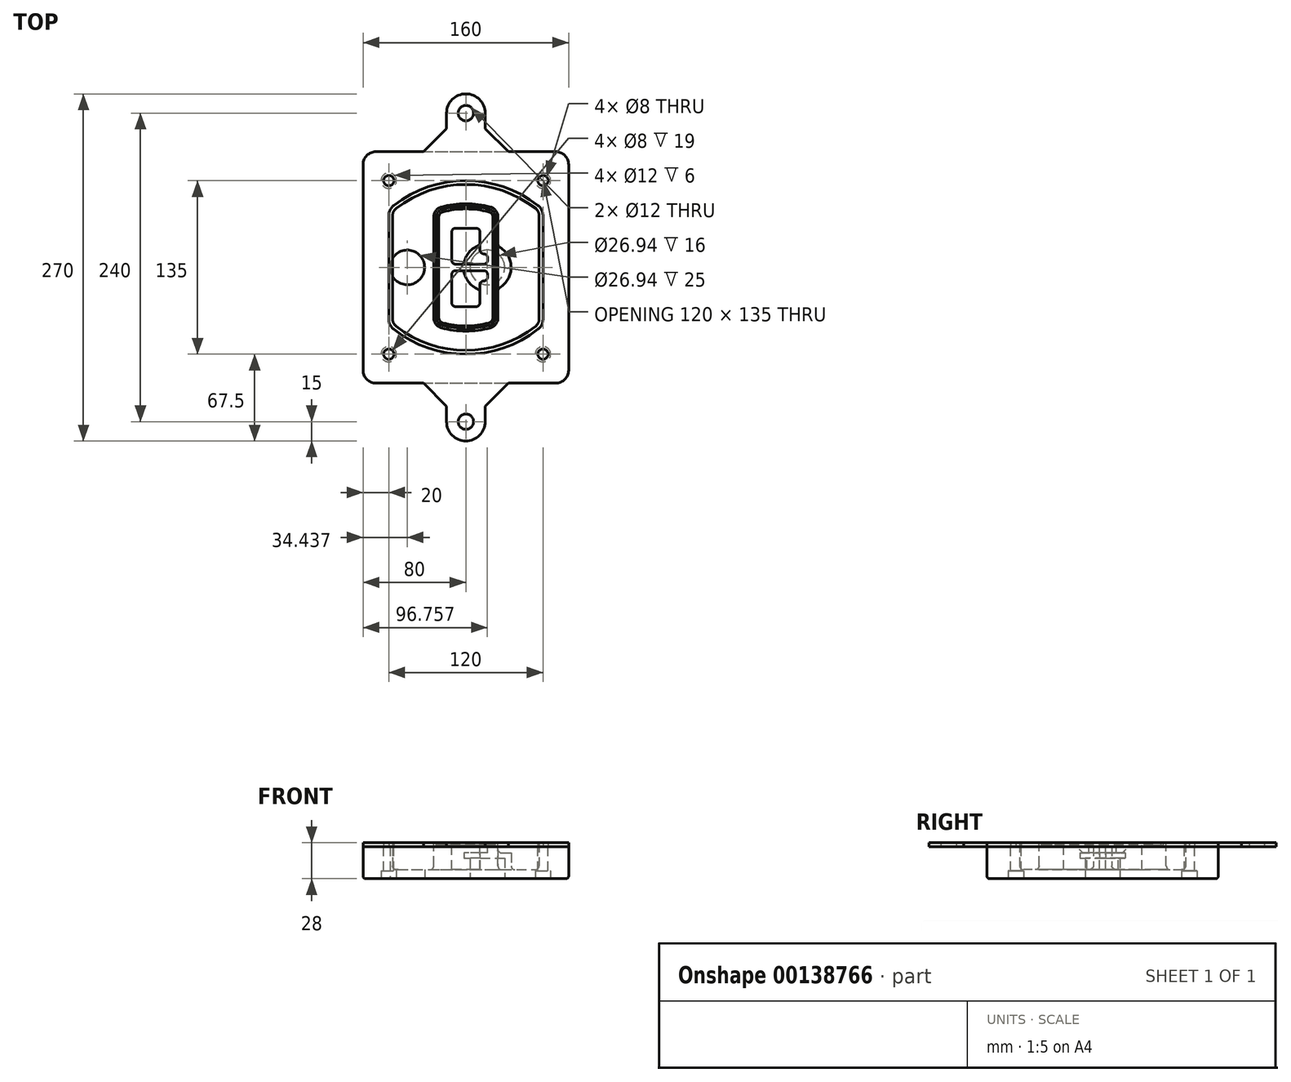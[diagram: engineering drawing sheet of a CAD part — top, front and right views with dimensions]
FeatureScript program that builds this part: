
annotation { "Feature Type Name" : "Feature", "Feature Type Description" : "" }
export const myFeature = defineFeature(function(context is Context, id is Id, definition is map)
    precondition{}
    {
        {
            var Q0;
            Q0=qCreatedBy(makeId("Top.planeOp"),FACE);
            var sketch = newSketch(context, id + "F0", { "sketchPlane" : qUnion([Q0])});
            skPoint(sketch, "E0.rect.middle", {"position": v(0, 0) * mm});
            skLineSegment(sketch, "E1.bottom", {"start": v(-70, -90) * mm, "end": v(70, -90) * mm});
            skLineSegment(sketch, "E1.top", {"start": v(-70, 90) * mm, "end": v(70, 90) * mm});
            skLineSegment(sketch, "E1.left", {"start": v(-80, -80) * mm, "end": v(-80, 80) * mm});
            skLineSegment(sketch, "E1.right", {"start": v(80, -80) * mm, "end": v(80, 80) * mm});
            skLineSegment(sketch, "E2", {"start": v(-80, 90) * mm, "end": v(80, -90) * mm, "construction": true});
            skLineSegment(sketch, "E3", {"start": v(80, 90) * mm, "end": v(-80, -90) * mm, "construction": true});
            skCircle(sketch, "E4", {"center": v(-60, 67.5) * mm, "radius": 4 * mm});
            skCircle(sketch, "E5", {"center": v(60, 67.5) * mm, "radius": 4 * mm});
            skCircle(sketch, "E6", {"center": v(60, -67.5) * mm, "radius": 4 * mm});
            skCircle(sketch, "E7", {"center": v(-60, -67.5) * mm, "radius": 4 * mm});
            skLineSegment(sketch, "E8", {"start": v(-60, 67.5) * mm, "end": v(60, 67.5) * mm, "construction": true});
            skLineSegment(sketch, "E9", {"start": v(60, 67.5) * mm, "end": v(60, -67.5) * mm, "construction": true});
            skLineSegment(sketch, "E10", {"start": v(60, -67.5) * mm, "end": v(-60, -67.5) * mm, "construction": true});
            skLineSegment(sketch, "E11", {"start": v(-60, -67.5) * mm, "end": v(-60, 67.5) * mm, "construction": true});
            skLineSegment(sketch, "E12", {"start": v(-60, 40.3) * mm, "end": v(-60, -40.3) * mm});
            skLineSegment(sketch, "E13", {"start": v(60, 40.3) * mm, "end": v(60, -40.3) * mm});
            skArc(sketch, "E14", {"start": v(56.15, 48.18) * mm, "mid": v(0, 67.5) * mm, "end": v(-56.15, 48.18) * mm});
            skArc(sketch, "E15", {"start": v(-56.15, -48.18) * mm, "mid": v(0, -67.5) * mm, "end": v(56.15, -48.18) * mm});
            skLineSegment(sketch, "E16", {"start": v(-60, 0) * mm, "end": v(60, 0) * mm, "construction": true});
            skPoint(sketch, "E17.visualSharp", {"position": v(-60, -45) * mm});
            skArc(sketch, "E17.filletArc", {"start": v(-60, -40.3) * mm, "mid": v(-58.99, -44.68) * mm, "end": v(-56.15, -48.18) * mm});
            skPoint(sketch, "E18.visualSharp", {"position": v(-60, 45) * mm});
            skArc(sketch, "E18.filletArc", {"start": v(-56.15, 48.18) * mm, "mid": v(-58.99, 44.68) * mm, "end": v(-60, 40.3) * mm});
            skPoint(sketch, "E19.visualSharp", {"position": v(60, 45) * mm});
            skArc(sketch, "E19.filletArc", {"start": v(60, 40.3) * mm, "mid": v(58.99, 44.68) * mm, "end": v(56.15, 48.18) * mm});
            skPoint(sketch, "E20.visualSharp", {"position": v(60, -45) * mm});
            skArc(sketch, "E20.filletArc", {"start": v(56.15, -48.18) * mm, "mid": v(58.99, -44.68) * mm, "end": v(60, -40.3) * mm});
            skPoint(sketch, "E21.visualSharp", {"position": v(-80, 90) * mm});
            skArc(sketch, "E21.filletArc", {"start": v(-70, 90) * mm, "mid": v(-77.07, 87.07) * mm, "end": v(-80, 80) * mm});
            skPoint(sketch, "E22.visualSharp", {"position": v(80, 90) * mm});
            skArc(sketch, "E22.filletArc", {"start": v(80, 80) * mm, "mid": v(77.07, 87.07) * mm, "end": v(70, 90) * mm});
            skPoint(sketch, "E23.visualSharp", {"position": v(80, -90) * mm});
            skArc(sketch, "E23.filletArc", {"start": v(70, -90) * mm, "mid": v(77.07, -87.07) * mm, "end": v(80, -80) * mm});
            skPoint(sketch, "E24.visualSharp", {"position": v(-80, -90) * mm});
            skArc(sketch, "E24.filletArc", {"start": v(-80, -80) * mm, "mid": v(-77.07, -87.07) * mm, "end": v(-70, -90) * mm});
            skArc(sketch, "E25.0", {"start": v(57, 40.3) * mm, "mid": v(56.3, 43.36) * mm, "end": v(54.3, 45.81) * mm});
            skLineSegment(sketch, "E25.1", {"start": v(57, 40.3) * mm, "end": v(57, -40.3) * mm});
            skArc(sketch, "E25.2", {"start": v(54.3, -45.81) * mm, "mid": v(56.3, -43.36) * mm, "end": v(57, -40.3) * mm});
            skArc(sketch, "E25.3", {"start": v(-54.3, -45.81) * mm, "mid": v(0, -64.5) * mm, "end": v(54.3, -45.81) * mm});
            skArc(sketch, "E25.4", {"start": v(-57, -40.3) * mm, "mid": v(-56.3, -43.36) * mm, "end": v(-54.3, -45.81) * mm});
            skArc(sketch, "E25.5", {"start": v(54.3, 45.81) * mm, "mid": v(0, 64.5) * mm, "end": v(-54.3, 45.81) * mm});
            skLineSegment(sketch, "E25.6", {"start": v(-57, 40.3) * mm, "end": v(-57, -40.3) * mm});
            skArc(sketch, "E25.7", {"start": v(-54.3, 45.81) * mm, "mid": v(-56.3, 43.36) * mm, "end": v(-57, 40.3) * mm});
            skArc(sketch, "E26.0", {"start": v(-58.62, 51.33) * mm, "mid": v(-62.58, 46.43) * mm, "end": v(-64, 40.3) * mm});
            skArc(sketch, "E26.1", {"start": v(58.62, 51.33) * mm, "mid": v(0, 71.5) * mm, "end": v(-58.62, 51.33) * mm});
            skArc(sketch, "E26.2", {"start": v(64, 40.3) * mm, "mid": v(62.58, 46.43) * mm, "end": v(58.62, 51.33) * mm});
            skLineSegment(sketch, "E26.3", {"start": v(64, 40.3) * mm, "end": v(64, -40.3) * mm});
            skArc(sketch, "E26.4", {"start": v(58.62, -51.33) * mm, "mid": v(62.58, -46.43) * mm, "end": v(64, -40.3) * mm});
            skLineSegment(sketch, "E26.5", {"start": v(-64, 40.3) * mm, "end": v(-64, -40.3) * mm});
            skArc(sketch, "E26.6", {"start": v(-58.62, -51.33) * mm, "mid": v(0, -71.5) * mm, "end": v(58.62, -51.33) * mm});
            skArc(sketch, "E26.7", {"start": v(-64, -40.3) * mm, "mid": v(-62.58, -46.43) * mm, "end": v(-58.62, -51.33) * mm});
            skSolve(sketch);
        }
        {
            var Q0;
            Q0=makeQuery(id+"F0.imprint","IMPRINT",FACE,{"disambiguationData":[TD([[makeQuery(id+"F0.imprint","IMPRINT",EDGE,{"derivedFrom":sQuery(id+"F0.wireOp",EDGE,"E1.bottom")}),1.0]])]});
            var Q1;
            Q1=makeQuery(id+"F0.imprint","IMPRINT",FACE,{"disambiguationData":[TD([[makeQuery(id+"F0.imprint","IMPRINT",EDGE,{"derivedFrom":sQuery(id+"F0.wireOp",EDGE,"E12")}),1.0]])]});
            var Q2;
            Q2=makeQuery(id+"F0.imprint","IMPRINT",FACE,{"disambiguationData":[TD([[makeQuery(id+"F0.imprint","IMPRINT",EDGE,{"derivedFrom":sQuery(id+"F0.wireOp",EDGE,"E25.0")}),1.0]])]});
            var Q3;
            Q3=makeQuery(id+"F0.imprint","IMPRINT",FACE,{"disambiguationData":[TD([[makeQuery(id+"F0.imprint","IMPRINT",EDGE,{"derivedFrom":sQuery(id+"F0.wireOp",EDGE,"E12")}),-1.0]])]});
            extrude(context, id + "F1", {"entities" : qUnion([Q0, Q1, Q2, Q3]), "oppositeDirection" : true, "depth" : 25 * mm});
        }
        {
            var Q0;
            Q0=makeQuery(id+"F0.imprint","IMPRINT",FACE,{"disambiguationData":[TD([[makeQuery(id+"F0.imprint","IMPRINT",EDGE,{"derivedFrom":sQuery(id+"F0.wireOp",EDGE,"E12")}),1.0]])]});
            extrude(context, id + "F2", {"entities" : qUnion([Q0]), "operationType" : NewBodyOperationType.ADD, "depth" : 3 * mm});
        }
        {
            var Q0;
            Q0=makeQuery(id+"F0.imprint","IMPRINT",FACE,{"disambiguationData":[TD([[makeQuery(id+"F0.imprint","IMPRINT",EDGE,{"derivedFrom":sQuery(id+"F0.wireOp",EDGE,"E25.0")}),1.0]])]});
            extrude(context, id + "F3", {"entities" : qUnion([Q0]), "operationType" : NewBodyOperationType.REMOVE, "oppositeDirection" : true, "depth" : 18 * mm});
        }
        {
            var Q0;
            Q0=makeQuery(id+"F2.opExtrude","CAP_FACE",FACE,{"disambiguationData":[OSD([sQuery(id+"F0.wireOp",EDGE,"E12"),sQuery(id+"F0.wireOp",EDGE,"E13"),sQuery(id+"F0.wireOp",EDGE,"E14"),sQuery(id+"F0.wireOp",EDGE,"E15"),sQuery(id+"F0.wireOp",EDGE,"E17.filletArc"),sQuery(id+"F0.wireOp",EDGE,"E18.filletArc"),sQuery(id+"F0.wireOp",EDGE,"E19.filletArc"),sQuery(id+"F0.wireOp",EDGE,"E20.filletArc"),sQuery(id+"F0.wireOp",EDGE,"E25.0"),sQuery(id+"F0.wireOp",EDGE,"E25.1"),sQuery(id+"F0.wireOp",EDGE,"E25.2"),sQuery(id+"F0.wireOp",EDGE,"E25.3"),sQuery(id+"F0.wireOp",EDGE,"E25.4"),sQuery(id+"F0.wireOp",EDGE,"E25.5"),sQuery(id+"F0.wireOp",EDGE,"E25.6"),sQuery(id+"F0.wireOp",EDGE,"E25.7")])],"isStart":false});
            var sketch = newSketch(context, id + "F4", { "sketchPlane" : qUnion([Q0])});
            skArc(sketch, "E27.0", {"start": v(-19.08, -46.97) * mm, "mid": v(0, -49.5) * mm, "end": v(19.08, -46.97) * mm});
            skArc(sketch, "E28.0", {"start": v(19.08, 46.97) * mm, "mid": v(0, 49.5) * mm, "end": v(-19.08, 46.97) * mm});
            skLineSegment(sketch, "E29", {"start": v(-25, 39.25) * mm, "end": v(-25, -39.25) * mm});
            skLineSegment(sketch, "E30", {"start": v(25, 39.25) * mm, "end": v(25, -39.25) * mm});
            skLineSegment(sketch, "E31", {"start": v(-25, 45.1) * mm, "end": v(25, 45.1) * mm, "construction": true});
            skLineSegment(sketch, "E32", {"start": v(-25, -45.1) * mm, "end": v(25, -45.1) * mm, "construction": true});
            skPoint(sketch, "E33.visualSharp", {"position": v(-25, 45.1) * mm});
            skArc(sketch, "E33.filletArc", {"start": v(-19.08, 46.97) * mm, "mid": v(-23.35, 44.11) * mm, "end": v(-25, 39.25) * mm});
            skPoint(sketch, "E34.visualSharp", {"position": v(25, 45.1) * mm});
            skArc(sketch, "E34.filletArc", {"start": v(25, 39.25) * mm, "mid": v(23.35, 44.11) * mm, "end": v(19.08, 46.97) * mm});
            skPoint(sketch, "E35.visualSharp", {"position": v(25, -45.1) * mm});
            skArc(sketch, "E35.filletArc", {"start": v(19.08, -46.97) * mm, "mid": v(23.35, -44.11) * mm, "end": v(25, -39.25) * mm});
            skPoint(sketch, "E36.visualSharp", {"position": v(-25, -45.1) * mm});
            skArc(sketch, "E36.filletArc", {"start": v(-25, -39.25) * mm, "mid": v(-23.35, -44.11) * mm, "end": v(-19.08, -46.97) * mm});
            skArc(sketch, "E37.0", {"start": v(54.3, 45.81) * mm, "mid": v(0, 64.5) * mm, "end": v(-54.3, 45.81) * mm});
            skArc(sketch, "E37.1", {"start": v(-54.3, 45.81) * mm, "mid": v(-56.3, 43.36) * mm, "end": v(-57, 40.3) * mm});
            skLineSegment(sketch, "E37.2", {"start": v(-57, 40.3) * mm, "end": v(-57, -40.3) * mm});
            skArc(sketch, "E37.3", {"start": v(-57, -40.3) * mm, "mid": v(-56.3, -43.36) * mm, "end": v(-54.3, -45.81) * mm});
            skArc(sketch, "E37.4", {"start": v(-54.3, -45.81) * mm, "mid": v(0, -64.5) * mm, "end": v(54.3, -45.81) * mm});
            skArc(sketch, "E37.5", {"start": v(54.3, -45.81) * mm, "mid": v(56.3, -43.36) * mm, "end": v(57, -40.3) * mm});
            skLineSegment(sketch, "E37.6", {"start": v(57, 40.3) * mm, "end": v(57, -40.3) * mm});
            skArc(sketch, "E37.7", {"start": v(57, 40.3) * mm, "mid": v(56.3, 43.36) * mm, "end": v(54.3, 45.81) * mm});
            skLineSegment(sketch, "E38.0", {"start": v(23, 39.25) * mm, "end": v(23, -39.25) * mm});
            skArc(sketch, "E38.1", {"start": v(18.56, -45.04) * mm, "mid": v(21.76, -42.9) * mm, "end": v(23, -39.25) * mm});
            skArc(sketch, "E38.2", {"start": v(-18.56, -45.04) * mm, "mid": v(0, -47.5) * mm, "end": v(18.56, -45.04) * mm});
            skArc(sketch, "E38.3", {"start": v(-23, -39.25) * mm, "mid": v(-21.76, -42.9) * mm, "end": v(-18.56, -45.04) * mm});
            skLineSegment(sketch, "E38.4", {"start": v(-23, 39.25) * mm, "end": v(-23, -39.25) * mm});
            skArc(sketch, "E38.5", {"start": v(23, 39.25) * mm, "mid": v(21.76, 42.9) * mm, "end": v(18.56, 45.04) * mm});
            skArc(sketch, "E38.6", {"start": v(-18.56, 45.04) * mm, "mid": v(-21.76, 42.9) * mm, "end": v(-23, 39.25) * mm});
            skArc(sketch, "E38.7", {"start": v(18.56, 45.04) * mm, "mid": v(0, 47.5) * mm, "end": v(-18.56, 45.04) * mm});
            skArc(sketch, "E39.0", {"start": v(21, 39.25) * mm, "mid": v(20.18, 41.68) * mm, "end": v(18.04, 43.1) * mm});
            skLineSegment(sketch, "E39.1", {"start": v(21, 39.25) * mm, "end": v(21, -39.25) * mm});
            skArc(sketch, "E39.2", {"start": v(18.04, -43.1) * mm, "mid": v(20.18, -41.68) * mm, "end": v(21, -39.25) * mm});
            skArc(sketch, "E39.3", {"start": v(-18.04, -43.1) * mm, "mid": v(0, -45.5) * mm, "end": v(18.04, -43.1) * mm});
            skArc(sketch, "E39.4", {"start": v(-21, -39.25) * mm, "mid": v(-20.18, -41.68) * mm, "end": v(-18.04, -43.1) * mm});
            skArc(sketch, "E39.5", {"start": v(18.04, 43.1) * mm, "mid": v(0, 45.5) * mm, "end": v(-18.04, 43.1) * mm});
            skLineSegment(sketch, "E39.6", {"start": v(-21, 39.25) * mm, "end": v(-21, -39.25) * mm});
            skArc(sketch, "E39.7", {"start": v(-18.04, 43.1) * mm, "mid": v(-20.18, 41.68) * mm, "end": v(-21, 39.25) * mm});
            skLineSegment(sketch, "E40", {"start": v(-25, 0) * mm, "end": v(25, 0) * mm, "construction": true});
            skLineSegment(sketch, "E41", {"start": v(-11, 5.5) * mm, "end": v(-11, 27.5) * mm});
            skLineSegment(sketch, "E42", {"start": v(-8, 30.5) * mm, "end": v(8, 30.5) * mm});
            skLineSegment(sketch, "E43", {"start": v(11, 27.5) * mm, "end": v(11, 13.5) * mm});
            skLineSegment(sketch, "E44", {"start": v(14, 10.5) * mm, "end": v(14, 10.5) * mm});
            skLineSegment(sketch, "E45", {"start": v(17, 7.5) * mm, "end": v(17, 5.5) * mm});
            skLineSegment(sketch, "E46", {"start": v(14, 2.5) * mm, "end": v(-8, 2.5) * mm});
            skPoint(sketch, "E47.visualSharp", {"position": v(-11, 30.5) * mm});
            skArc(sketch, "E47.filletArc", {"start": v(-8, 30.5) * mm, "mid": v(-10.12, 29.62) * mm, "end": v(-11, 27.5) * mm});
            skPoint(sketch, "E48.visualSharp", {"position": v(11, 30.5) * mm});
            skArc(sketch, "E48.filletArc", {"start": v(11, 27.5) * mm, "mid": v(10.12, 29.62) * mm, "end": v(8, 30.5) * mm});
            skPoint(sketch, "E49.visualSharp", {"position": v(11, 10.5) * mm});
            skArc(sketch, "E49.filletArc", {"start": v(11, 13.5) * mm, "mid": v(11.88, 11.38) * mm, "end": v(14, 10.5) * mm});
            skPoint(sketch, "E50.visualSharp", {"position": v(17, 10.5) * mm});
            skArc(sketch, "E50.filletArc", {"start": v(17, 7.5) * mm, "mid": v(16.12, 9.62) * mm, "end": v(14, 10.5) * mm});
            skPoint(sketch, "E51.visualSharp", {"position": v(17, 2.5) * mm});
            skArc(sketch, "E51.filletArc", {"start": v(14, 2.5) * mm, "mid": v(16.12, 3.38) * mm, "end": v(17, 5.5) * mm});
            skPoint(sketch, "E52.visualSharp", {"position": v(-11, 2.5) * mm});
            skArc(sketch, "E52.filletArc", {"start": v(-11, 5.5) * mm, "mid": v(-10.12, 3.38) * mm, "end": v(-8, 2.5) * mm});
            skLineSegment(sketch, "E53.0.MirrorCS", {"start": v(14, -2.5) * mm, "end": v(-8, -2.5) * mm});
            skArc(sketch, "E54.0.MirrorCS", {"start": v(-11, -5.5) * mm, "mid": v(-10.12, -3.38) * mm, "end": v(-8, -2.5) * mm});
            skLineSegment(sketch, "E55.0.MirrorCS", {"start": v(-11, -5.5) * mm, "end": v(-11, -27.5) * mm});
            skArc(sketch, "E56.0.MirrorCS", {"start": v(-8, -30.5) * mm, "mid": v(-10.12, -29.62) * mm, "end": v(-11, -27.5) * mm});
            skLineSegment(sketch, "E57.0.MirrorCS", {"start": v(-8, -30.5) * mm, "end": v(8, -30.5) * mm});
            skArc(sketch, "E58.0.MirrorCS", {"start": v(11, -27.5) * mm, "mid": v(10.12, -29.62) * mm, "end": v(8, -30.5) * mm});
            skLineSegment(sketch, "E59.0.MirrorCS", {"start": v(11, -27.5) * mm, "end": v(11, -13.5) * mm});
            skArc(sketch, "E60.0.MirrorCS", {"start": v(11, -13.5) * mm, "mid": v(11.88, -11.38) * mm, "end": v(14, -10.5) * mm});
            skArc(sketch, "E61.0.MirrorCS", {"start": v(17, -7.5) * mm, "mid": v(16.12, -9.62) * mm, "end": v(14, -10.5) * mm});
            skLineSegment(sketch, "E62.0.MirrorCS", {"start": v(17, -7.5) * mm, "end": v(17, -5.5) * mm});
            skArc(sketch, "E63.0.MirrorCS", {"start": v(14, -2.5) * mm, "mid": v(16.12, -3.38) * mm, "end": v(17, -5.5) * mm});
            skSolve(sketch);
        }
        {
            var Q0;
            Q0=makeQuery(id+"F4.imprint","IMPRINT",FACE,{"disambiguationData":[TD([[makeQuery(id+"F4.imprint","IMPRINT",EDGE,{"derivedFrom":sQuery(id+"F4.wireOp",EDGE,"E27.0")}),1.0]])]});
            var Q1;
            Q1=makeQuery(id+"F4.imprint","IMPRINT",FACE,{"disambiguationData":[TD([[makeQuery(id+"F4.imprint","IMPRINT",EDGE,{"derivedFrom":sQuery(id+"F4.wireOp",EDGE,"E38.0")}),-1.0]])]});
            var Q2;
            Q2=makeQuery(id+"F4.imprint","IMPRINT",FACE,{"disambiguationData":[TD([[makeQuery(id+"F4.imprint","IMPRINT",EDGE,{"derivedFrom":sQuery(id+"F4.wireOp",EDGE,"E39.0")}),1.0]])]});
            extrude(context, id + "F5", {"entities" : qUnion([Q0, Q1, Q2]), "operationType" : NewBodyOperationType.ADD, "endBound" : BoundingType.UP_TO_NEXT, "oppositeDirection" : true, "depth" : 25 * mm});
        }
        {
            var Q0;
            Q0=makeQuery(id+"F4.imprint","IMPRINT",FACE,{"disambiguationData":[TD([[makeQuery(id+"F4.imprint","IMPRINT",EDGE,{"derivedFrom":sQuery(id+"F4.wireOp",EDGE,"E38.0")}),-1.0]])]});
            extrude(context, id + "F6", {"entities" : qUnion([Q0]), "operationType" : NewBodyOperationType.REMOVE, "oppositeDirection" : true, "depth" : 2 * mm});
        }
        {
            var Q0;
            Q0=makeQuery(id+"F1.opExtrude","CAP_FACE",FACE,{"disambiguationData":[OSD([sQuery(id+"F0.wireOp",EDGE,"E1.bottom"),sQuery(id+"F0.wireOp",EDGE,"E1.top"),sQuery(id+"F0.wireOp",EDGE,"E1.left"),sQuery(id+"F0.wireOp",EDGE,"E1.right"),sQuery(id+"F0.wireOp",EDGE,"E4"),sQuery(id+"F0.wireOp",EDGE,"E5"),sQuery(id+"F0.wireOp",EDGE,"E6"),sQuery(id+"F0.wireOp",EDGE,"E7"),sQuery(id+"F0.wireOp",EDGE,"E21.filletArc"),sQuery(id+"F0.wireOp",EDGE,"E22.filletArc"),sQuery(id+"F0.wireOp",EDGE,"E23.filletArc"),sQuery(id+"F0.wireOp",EDGE,"E24.filletArc")])],"isStart":false});
            var sketch = newSketch(context, id + "F7", { "sketchPlane" : qUnion([Q0])});
            skCircle(sketch, "E64", {"center": v(16.76, 0) * mm, "radius": 13.47 * mm});
            skCircle(sketch, "E65", {"center": v(-45.56, 0) * mm, "radius": 13.47 * mm});
            skLineSegment(sketch, "E66", {"start": v(80, 0) * mm, "end": v(-80, 0) * mm});
            skCircle(sketch, "E67", {"center": v(16.76, 0) * mm, "radius": 18.47 * mm});
            skCircle(sketch, "E68", {"center": v(60, -67.5) * mm, "radius": 6 * mm});
            skCircle(sketch, "E69", {"center": v(-60, -67.5) * mm, "radius": 6 * mm});
            skCircle(sketch, "E70", {"center": v(-60, 67.5) * mm, "radius": 6 * mm});
            skCircle(sketch, "E71", {"center": v(60, 67.5) * mm, "radius": 6 * mm});
            skSolve(sketch);
        }
        {
            var Q0;
            {var subQ1=sQuery(id+"F7.wireOp",EDGE,"E66");var subQ4=sQuery(id+"F7.wireOp",EDGE,"E64");var subQ6=makeQuery(id+"F7.imprint","INTERSECT",VERTEX,{"disambiguationData":[OD(0.0)],"derivedFrom":[subQ4,subQ1]});Q0=makeQuery(id+"F7.imprint","IMPRINT",FACE,{"disambiguationData":[TD([[makeQuery(id+"F7.imprint","IMPRINT",EDGE,{"disambiguationData":[TD([[subQ6,-1.0]])],"derivedFrom":subQ4}),-1.0]])]});}
            var Q1;
            {var subQ0=sQuery(id+"F7.wireOp",EDGE,"E66");var subQ1=sQuery(id+"F7.wireOp",EDGE,"E64");var subQ3=makeQuery(id+"F7.imprint","INTERSECT",VERTEX,{"disambiguationData":[OD(0.0)],"derivedFrom":[subQ1,subQ0]});Q1=makeQuery(id+"F7.imprint","IMPRINT",FACE,{"disambiguationData":[TD([[makeQuery(id+"F7.imprint","IMPRINT",EDGE,{"disambiguationData":[TD([[subQ3,-1.0]])],"derivedFrom":subQ1}),1.0]])]});}
            var Q2;
            {var subQ0=sQuery(id+"F7.wireOp",EDGE,"E66");var subQ1=sQuery(id+"F7.wireOp",EDGE,"E64");var subQ3=makeQuery(id+"F7.imprint","INTERSECT",VERTEX,{"disambiguationData":[OD(0.0)],"derivedFrom":[subQ1,subQ0]});Q2=makeQuery(id+"F7.imprint","IMPRINT",FACE,{"disambiguationData":[TD([[makeQuery(id+"F7.imprint","IMPRINT",EDGE,{"disambiguationData":[TD([[subQ3,1.0]])],"derivedFrom":subQ1}),1.0]])]});}
            var Q3;
            {var subQ1=sQuery(id+"F7.wireOp",EDGE,"E66");var subQ4=sQuery(id+"F7.wireOp",EDGE,"E64");var subQ6=makeQuery(id+"F7.imprint","INTERSECT",VERTEX,{"disambiguationData":[OD(0.0)],"derivedFrom":[subQ4,subQ1]});Q3=makeQuery(id+"F7.imprint","IMPRINT",FACE,{"disambiguationData":[TD([[makeQuery(id+"F7.imprint","IMPRINT",EDGE,{"disambiguationData":[TD([[subQ6,1.0]])],"derivedFrom":subQ4}),-1.0]])]});}
            extrude(context, id + "F8", {"entities" : qUnion([Q0, Q1, Q2, Q3]), "operationType" : NewBodyOperationType.ADD, "oppositeDirection" : true, "depth" : 20 * mm});
        }
        {
            var Q0;
            {var subQ0=sQuery(id+"F7.wireOp",EDGE,"E66");var subQ1=sQuery(id+"F7.wireOp",EDGE,"E64");var subQ3=makeQuery(id+"F7.imprint","INTERSECT",VERTEX,{"disambiguationData":[OD(0.0)],"derivedFrom":[subQ1,subQ0]});Q0=makeQuery(id+"F7.imprint","IMPRINT",FACE,{"disambiguationData":[TD([[makeQuery(id+"F7.imprint","IMPRINT",EDGE,{"disambiguationData":[TD([[subQ3,-1.0]])],"derivedFrom":subQ1}),1.0]])]});}
            var Q1;
            {var subQ0=sQuery(id+"F7.wireOp",EDGE,"E66");var subQ1=sQuery(id+"F7.wireOp",EDGE,"E64");var subQ3=makeQuery(id+"F7.imprint","INTERSECT",VERTEX,{"disambiguationData":[OD(0.0)],"derivedFrom":[subQ1,subQ0]});Q1=makeQuery(id+"F7.imprint","IMPRINT",FACE,{"disambiguationData":[TD([[makeQuery(id+"F7.imprint","IMPRINT",EDGE,{"disambiguationData":[TD([[subQ3,1.0]])],"derivedFrom":subQ1}),1.0]])]});}
            extrude(context, id + "F9", {"entities" : qUnion([Q0, Q1]), "operationType" : NewBodyOperationType.REMOVE, "oppositeDirection" : true, "depth" : 16 * mm});
        }
        {
            var Q0;
            {var subQ0=sQuery(id+"F7.wireOp",EDGE,"E66");var subQ1=sQuery(id+"F7.wireOp",EDGE,"E65");var subQ3=makeQuery(id+"F7.imprint","INTERSECT",VERTEX,{"disambiguationData":[OD(0.0)],"derivedFrom":[subQ1,subQ0]});Q0=makeQuery(id+"F7.imprint","IMPRINT",FACE,{"disambiguationData":[TD([[makeQuery(id+"F7.imprint","IMPRINT",EDGE,{"disambiguationData":[TD([[subQ3,-1.0]])],"derivedFrom":subQ1}),1.0]])]});}
            var Q1;
            {var subQ0=sQuery(id+"F7.wireOp",EDGE,"E66");var subQ1=sQuery(id+"F7.wireOp",EDGE,"E65");var subQ3=makeQuery(id+"F7.imprint","INTERSECT",VERTEX,{"disambiguationData":[OD(0.0)],"derivedFrom":[subQ1,subQ0]});Q1=makeQuery(id+"F7.imprint","IMPRINT",FACE,{"disambiguationData":[TD([[makeQuery(id+"F7.imprint","IMPRINT",EDGE,{"disambiguationData":[TD([[subQ3,1.0]])],"derivedFrom":subQ1}),1.0]])]});}
            extrude(context, id + "F10", {"entities" : qUnion([Q0, Q1]), "operationType" : NewBodyOperationType.REMOVE, "oppositeDirection" : true, "depth" : 25 * mm});
        }
        {
            var Q0;
            Q0=makeQuery(id+"F7.imprint","IMPRINT",FACE,{"disambiguationData":[TD([[makeQuery(id+"F7.imprint","IMPRINT",EDGE,{"derivedFrom":sQuery(id+"F7.wireOp",EDGE,"E68")}),1.0]])]});
            var Q1;
            Q1=makeQuery(id+"F7.imprint","IMPRINT",FACE,{"disambiguationData":[TD([[makeQuery(id+"F7.imprint","IMPRINT",EDGE,{"derivedFrom":makeQuery(id+"F1.opExtrude","CAP_EDGE",EDGE,{"disambiguationData":[OSD([sQuery(id+"F0.wireOp",EDGE,"E5")])],"isStart":false})}),-1.0]])]});
            var Q2;
            Q2=makeQuery(id+"F7.imprint","IMPRINT",FACE,{"disambiguationData":[TD([[makeQuery(id+"F7.imprint","IMPRINT",EDGE,{"derivedFrom":sQuery(id+"F7.wireOp",EDGE,"E69")}),1.0]])]});
            var Q3;
            Q3=makeQuery(id+"F7.imprint","IMPRINT",FACE,{"disambiguationData":[TD([[makeQuery(id+"F7.imprint","IMPRINT",EDGE,{"derivedFrom":makeQuery(id+"F1.opExtrude","CAP_EDGE",EDGE,{"disambiguationData":[OSD([sQuery(id+"F0.wireOp",EDGE,"E4")])],"isStart":false})}),-1.0]])]});
            var Q4;
            Q4=makeQuery(id+"F7.imprint","IMPRINT",FACE,{"disambiguationData":[TD([[makeQuery(id+"F7.imprint","IMPRINT",EDGE,{"derivedFrom":sQuery(id+"F7.wireOp",EDGE,"E70")}),1.0]])]});
            var Q5;
            Q5=makeQuery(id+"F7.imprint","IMPRINT",FACE,{"disambiguationData":[TD([[makeQuery(id+"F7.imprint","IMPRINT",EDGE,{"derivedFrom":makeQuery(id+"F1.opExtrude","CAP_EDGE",EDGE,{"disambiguationData":[OSD([sQuery(id+"F0.wireOp",EDGE,"E7")])],"isStart":false})}),-1.0]])]});
            var Q6;
            Q6=makeQuery(id+"F7.imprint","IMPRINT",FACE,{"disambiguationData":[TD([[makeQuery(id+"F7.imprint","IMPRINT",EDGE,{"derivedFrom":sQuery(id+"F7.wireOp",EDGE,"E71")}),1.0]])]});
            var Q7;
            Q7=makeQuery(id+"F7.imprint","IMPRINT",FACE,{"disambiguationData":[TD([[makeQuery(id+"F7.imprint","IMPRINT",EDGE,{"derivedFrom":makeQuery(id+"F1.opExtrude","CAP_EDGE",EDGE,{"disambiguationData":[OSD([sQuery(id+"F0.wireOp",EDGE,"E6")])],"isStart":false})}),-1.0]])]});
            extrude(context, id + "F11", {"entities" : qUnion([Q0, Q1, Q2, Q3, Q4, Q5, Q6, Q7]), "operationType" : NewBodyOperationType.REMOVE, "oppositeDirection" : true, "depth" : 6 * mm});
        }
        {
            var Q0;
            Q0=makeQuery(id+"F9.boolean.opBoolean","COPY",FACE,{"derivedFrom":makeQuery(id+"F9.opExtrude","CAP_FACE",FACE,{"disambiguationData":[OSD([sQuery(id+"F7.wireOp",EDGE,"E64")])],"isStart":false})});
            var sketch = newSketch(context, id + "F12", { "sketchPlane" : qUnion([Q0])});
            skArc(sketch, "E72.0", {"start": v(11, 17.55) * mm, "mid": v(2.57, 11.82) * mm, "end": v(-1.54, 2.5) * mm});
            skArc(sketch, "E72.1", {"start": v(-1.54, -2.5) * mm, "mid": v(2.57, -11.82) * mm, "end": v(11, -17.55) * mm});
            skLineSegment(sketch, "E73", {"start": v(-1.54, -2.5) * mm, "end": v(14, -2.5) * mm});
            skLineSegment(sketch, "E74.0", {"start": v(14, 2.5) * mm, "end": v(-1.54, 2.5) * mm});
            skArc(sketch, "E74.1", {"start": v(14, 2.5) * mm, "mid": v(16.12, 3.38) * mm, "end": v(17, 5.5) * mm});
            skLineSegment(sketch, "E74.2", {"start": v(17, 7.5) * mm, "end": v(17, 5.5) * mm});
            skArc(sketch, "E74.3", {"start": v(17, 7.5) * mm, "mid": v(16.12, 9.62) * mm, "end": v(14, 10.5) * mm});
            skArc(sketch, "E74.4", {"start": v(11, 13.5) * mm, "mid": v(11.88, 11.38) * mm, "end": v(14, 10.5) * mm});
            skLineSegment(sketch, "E74.5", {"start": v(11, 17.55) * mm, "end": v(11, 13.5) * mm});
            skLineSegment(sketch, "E74.7", {"start": v(14, -2.5) * mm, "end": v(-1.54, -2.5) * mm});
            skArc(sketch, "E74.8", {"start": v(14, -2.5) * mm, "mid": v(16.12, -3.38) * mm, "end": v(17, -5.5) * mm});
            skLineSegment(sketch, "E74.9", {"start": v(17, -7.5) * mm, "end": v(17, -5.5) * mm});
            skArc(sketch, "E74.10", {"start": v(17, -7.5) * mm, "mid": v(16.12, -9.62) * mm, "end": v(14, -10.5) * mm});
            skArc(sketch, "E74.11", {"start": v(11, -13.5) * mm, "mid": v(11.88, -11.38) * mm, "end": v(14, -10.5) * mm});
            skLineSegment(sketch, "E74.12", {"start": v(11, -17.55) * mm, "end": v(11, -13.5) * mm});
            skPoint(sketch, "E75.orphan", {"position": v(11, -27.5) * mm});
            skPoint(sketch, "E76.orphan", {"position": v(-8, -2.5) * mm});
            skPoint(sketch, "E77.orphan", {"position": v(-8, 2.5) * mm});
            skPoint(sketch, "E78.orphan", {"position": v(11, 27.5) * mm});
            skSolve(sketch);
        }
        {
            var Q0;
            {var subQ7=sQuery(id+"F12.wireOp",EDGE,"E72.0");var subQ14=sQuery(id+"F12.wireOp",EDGE,"E72.1");var subQ16=sQuery(id+"F12.wireOp",EDGE,"E74.1");var subQ18=sQuery(id+"F12.wireOp",EDGE,"E74.8");Q0=qUnion([makeQuery(id+"F12.imprint","IMPRINT",FACE,{"disambiguationData":[TD([[makeQuery(id+"F12.imprint","IMPRINT",EDGE,{"derivedFrom":subQ7}),1.0]])]}),makeQuery(id+"F12.imprint","IMPRINT",FACE,{"disambiguationData":[TD([[makeQuery(id+"F12.imprint","IMPRINT",EDGE,{"derivedFrom":subQ14}),1.0]])]}),makeQuery(id+"F12.imprint","IMPRINT",FACE,{"disambiguationData":[TD([[makeQuery(id+"F12.imprint","IMPRINT",EDGE,{"derivedFrom":subQ16}),1.0]])]}),makeQuery(id+"F12.imprint","IMPRINT",FACE,{"disambiguationData":[TD([[makeQuery(id+"F12.imprint","IMPRINT",EDGE,{"derivedFrom":subQ18}),-1.0]])]})]);}
            var Q1;
            Q1=makeQuery(id+"F5.boolean.opBoolean","SPLIT",FACE,{"disambiguationData":[TD([makeQuery(id+"F5.opExtrude","SWEPT_FACE",FACE,{"disambiguationData":[OSD([sQuery(id+"F4.wireOp",EDGE,"E41")])]})])],"derivedFrom":makeQuery(id+"F3.boolean.opBoolean","COPY",FACE,{"derivedFrom":makeQuery(id+"F3.opExtrude","CAP_FACE",FACE,{"disambiguationData":[OSD([sQuery(id+"F0.wireOp",EDGE,"E25.0"),sQuery(id+"F0.wireOp",EDGE,"E25.1"),sQuery(id+"F0.wireOp",EDGE,"E25.2"),sQuery(id+"F0.wireOp",EDGE,"E25.3"),sQuery(id+"F0.wireOp",EDGE,"E25.4"),sQuery(id+"F0.wireOp",EDGE,"E25.5"),sQuery(id+"F0.wireOp",EDGE,"E25.6"),sQuery(id+"F0.wireOp",EDGE,"E25.7")])],"isStart":false})})});
            extrude(context, id + "F13", {"entities" : qUnion([Q0]), "operationType" : NewBodyOperationType.REMOVE, "endBound" : BoundingType.UP_TO_SURFACE, "endBoundEntityFace" : qUnion([Q1]), "depth" : 25 * mm});
        }
        {
            var Q0;
            Q0=makeQuery(id+"F3.boolean.opBoolean","COPY",EDGE,{"derivedFrom":makeQuery(id+"F3.opExtrude","CAP_EDGE",EDGE,{"disambiguationData":[OSD([sQuery(id+"F0.wireOp",EDGE,"E25.6")])],"isStart":false})});
            var Q1;
            Q1=makeQuery(id+"F8.boolean.opBoolean","INTERSECT",EDGE,{"derivedFrom":[makeQuery(id+"F5.opExtrude","SWEPT_FACE",FACE,{"disambiguationData":[OSD([sQuery(id+"F4.wireOp",EDGE,"E30")])]}),makeQuery(id+"F8.opExtrude","CAP_FACE",FACE,{"disambiguationData":[OSD([sQuery(id+"F7.wireOp",EDGE,"E67")])],"isStart":false})]});
            var Q2;
            Q2=makeQuery(id+"F8.boolean.opBoolean","INTERSECT",EDGE,{"disambiguationData":[OD(1.0)],"derivedFrom":[makeQuery(id+"F5.opExtrude","SWEPT_FACE",FACE,{"disambiguationData":[OSD([sQuery(id+"F4.wireOp",EDGE,"E30")])]}),makeQuery(id+"F8.opExtrude","SWEPT_FACE",FACE,{"disambiguationData":[OSD([sQuery(id+"F7.wireOp",EDGE,"E67")])]})]});
            var Q3;
            {var subQ0=sQuery(id+"F4.wireOp",EDGE,"E30");Q3=makeQuery(id+"F8.boolean.opBoolean","SPLIT",EDGE,{"disambiguationData":[TD([makeQuery(id+"F5.opExtrude","SWEPT_FACE",FACE,{"disambiguationData":[OSD([sQuery(id+"F4.wireOp",EDGE,"E35.filletArc")])]})])],"derivedFrom":makeQuery(id+"F5.opExtrude","CAP_EDGE",EDGE,{"disambiguationData":[OSD([subQ0])],"isStart":false})});}
            var Q4;
            {var subQ0=sQuery(id+"F0.wireOp",EDGE,"E25.7");var subQ1=sQuery(id+"F0.wireOp",EDGE,"E25.1");var subQ2=sQuery(id+"F0.wireOp",EDGE,"E25.6");var subQ3=sQuery(id+"F0.wireOp",EDGE,"E25.5");var subQ4=sQuery(id+"F0.wireOp",EDGE,"E25.4");var subQ5=sQuery(id+"F0.wireOp",EDGE,"E25.0");var subQ6=sQuery(id+"F0.wireOp",EDGE,"E25.2");var subQ7=sQuery(id+"F0.wireOp",EDGE,"E25.3");Q4=makeQuery(id+"F8.boolean.opBoolean","INTERSECT",EDGE,{"derivedFrom":[makeQuery(id+"F5.boolean.opBoolean","SPLIT",FACE,{"disambiguationData":[TD([makeQuery(id+"F2.opExtrude","SWEPT_FACE",FACE,{"disambiguationData":[OSD([subQ5])]})])],"derivedFrom":makeQuery(id+"F3.boolean.opBoolean","COPY",FACE,{"derivedFrom":makeQuery(id+"F3.opExtrude","CAP_FACE",FACE,{"disambiguationData":[OSD([subQ5,subQ1,subQ6,subQ7,subQ4,subQ3,subQ2,subQ0])],"isStart":false})})}),makeQuery(id+"F8.opExtrude","SWEPT_FACE",FACE,{"disambiguationData":[OSD([sQuery(id+"F7.wireOp",EDGE,"E67")])]})]});}
            var Q5;
            Q5=makeQuery(id+"F8.boolean.opBoolean","INTERSECT",EDGE,{"disambiguationData":[OD(0.0)],"derivedFrom":[makeQuery(id+"F5.opExtrude","SWEPT_FACE",FACE,{"disambiguationData":[OSD([sQuery(id+"F4.wireOp",EDGE,"E30")])]}),makeQuery(id+"F8.opExtrude","SWEPT_FACE",FACE,{"disambiguationData":[OSD([sQuery(id+"F7.wireOp",EDGE,"E67")])]})]});
            fillet(context, id + "F14", {"entities" : qUnion([Q0, Q1, Q2, Q3, Q4, Q5]), "radius" : 3 * mm, "tangentPropagation" : true, "allowEdgeOverflow" : false});
        }
        {
            var Q0;
            Q0=makeQuery(id+"F1.opExtrude","CAP_EDGE",EDGE,{"disambiguationData":[OSD([sQuery(id+"F0.wireOp",EDGE,"E1.bottom")])],"isStart":false});
            fillet(context, id + "F15", {"entities" : qUnion([Q0]), "radius" : 2 * mm, "tangentPropagation" : true, "allowEdgeOverflow" : false});
        }
        {
            var Q0;
            {var subQ0=sQuery(id+"F0.wireOp",EDGE,"E22.filletArc");var subQ1=sQuery(id+"F0.wireOp",EDGE,"E7");var subQ2=sQuery(id+"F0.wireOp",EDGE,"E6");var subQ3=sQuery(id+"F0.wireOp",EDGE,"E5");var subQ4=sQuery(id+"F0.wireOp",EDGE,"E4");var subQ5=sQuery(id+"F0.wireOp",EDGE,"E1.bottom");var subQ6=sQuery(id+"F0.wireOp",EDGE,"E21.filletArc");var subQ7=sQuery(id+"F0.wireOp",EDGE,"E1.top");var subQ8=sQuery(id+"F0.wireOp",EDGE,"E1.left");var subQ9=sQuery(id+"F0.wireOp",EDGE,"E1.right");var subQ10=sQuery(id+"F0.wireOp",EDGE,"E23.filletArc");var subQ11=sQuery(id+"F0.wireOp",EDGE,"E24.filletArc");Q0=makeQuery(id+"F2.boolean.opBoolean","SPLIT",FACE,{"disambiguationData":[TD([makeQuery(id+"F1.opExtrude","SWEPT_FACE",FACE,{"disambiguationData":[OSD([subQ5])]})])],"derivedFrom":makeQuery(id+"F1.opExtrude","CAP_FACE",FACE,{"disambiguationData":[OSD([subQ5,subQ7,subQ8,subQ9,subQ4,subQ3,subQ2,subQ1,subQ6,subQ0,subQ10,subQ11])],"isStart":true})});}
            var sketch = newSketch(context, id + "F16", { "sketchPlane" : qUnion([Q0])});
            skLineSegment(sketch, "E79", {"start": v(0, 90) * mm, "end": v(0, 120) * mm, "construction": true});
            skPoint(sketch, "E79.endSnap0", {"position": v(0, 90) * mm});
            skLineSegment(sketch, "E80", {"start": v(-33, 90) * mm, "end": v(-15, 108) * mm});
            skLineSegment(sketch, "E81", {"start": v(-15, 108) * mm, "end": v(-15, 120) * mm});
            skLineSegment(sketch, "E82", {"start": v(33, 90) * mm, "end": v(15, 108) * mm});
            skLineSegment(sketch, "E83", {"start": v(15, 108) * mm, "end": v(15, 120) * mm});
            skArc(sketch, "E84", {"start": v(15, 120) * mm, "mid": v(0, 135) * mm, "end": v(-15, 120) * mm});
            skCircle(sketch, "E85", {"center": v(0, 120) * mm, "radius": 6 * mm});
            skLineSegment(sketch, "E86", {"start": v(-80, 0) * mm, "end": v(80, 0) * mm, "construction": true});
            skLineSegment(sketch, "E87.MirrorCS", {"start": v(-15, -108) * mm, "end": v(-15, -120) * mm});
            skLineSegment(sketch, "E88.MirrorCS", {"start": v(15, -108) * mm, "end": v(15, -120) * mm});
            skLineSegment(sketch, "E89.MirrorCS", {"start": v(-33, -90) * mm, "end": v(-15, -108) * mm});
            skArc(sketch, "E90.MirrorCS", {"start": v(15, -120) * mm, "mid": v(0, -135) * mm, "end": v(-15, -120) * mm});
            skCircle(sketch, "E91.MirrorC", {"center": v(0, -120) * mm, "radius": 6 * mm});
            skLineSegment(sketch, "E92.MirrorCS", {"start": v(0, -90) * mm, "end": v(0, -120) * mm, "construction": true});
            skLineSegment(sketch, "E93.MirrorCS", {"start": v(33, -90) * mm, "end": v(15, -108) * mm});
            skPoint(sketch, "E94.MirrorP", {"position": v(0, -90) * mm});
            skSolve(sketch);
        }
        {
            var Q0;
            {var subQ1=sQuery(id+"F16.wireOp",EDGE,"E80");Q0=makeQuery(id+"F16.imprint","IMPRINT",FACE,{"disambiguationData":[TD([[makeQuery(id+"F16.imprint","IMPRINT",EDGE,{"derivedFrom":subQ1}),-1.0]])]});}
            var Q1;
            Q1=makeQuery(id+"F16.imprint","IMPRINT",FACE,{"disambiguationData":[TD([[makeQuery(id+"F16.imprint","IMPRINT",EDGE,{"derivedFrom":sQuery(id+"F16.wireOp",EDGE,"E87.MirrorCS")}),1.0]])]});
            var Q2;
            Q2=makeQuery(id+"F16.imprint","IMPRINT",FACE,{"disambiguationData":[TD([[makeQuery(id+"F16.imprint","IMPRINT",EDGE,{"derivedFrom":makeQuery(id+"F1.opExtrude","CAP_EDGE",EDGE,{"disambiguationData":[OSD([sQuery(id+"F0.wireOp",EDGE,"E1.left")])],"isStart":true})}),-1.0]])]});
            var Q3;
            Q3=makeQuery(id+"F2.opExtrude","CAP_FACE",FACE,{"disambiguationData":[OSD([sQuery(id+"F0.wireOp",EDGE,"E12"),sQuery(id+"F0.wireOp",EDGE,"E13"),sQuery(id+"F0.wireOp",EDGE,"E14"),sQuery(id+"F0.wireOp",EDGE,"E15"),sQuery(id+"F0.wireOp",EDGE,"E17.filletArc"),sQuery(id+"F0.wireOp",EDGE,"E18.filletArc"),sQuery(id+"F0.wireOp",EDGE,"E19.filletArc"),sQuery(id+"F0.wireOp",EDGE,"E20.filletArc"),sQuery(id+"F0.wireOp",EDGE,"E25.0"),sQuery(id+"F0.wireOp",EDGE,"E25.1"),sQuery(id+"F0.wireOp",EDGE,"E25.2"),sQuery(id+"F0.wireOp",EDGE,"E25.3"),sQuery(id+"F0.wireOp",EDGE,"E25.4"),sQuery(id+"F0.wireOp",EDGE,"E25.5"),sQuery(id+"F0.wireOp",EDGE,"E25.6"),sQuery(id+"F0.wireOp",EDGE,"E25.7")])],"isStart":false});
            extrude(context, id + "F17", {"entities" : qUnion([Q0, Q1, Q2]), "endBound" : BoundingType.UP_TO_SURFACE, "endBoundEntityFace" : qUnion([Q3]), "depth" : 25 * mm});
        }
    });
